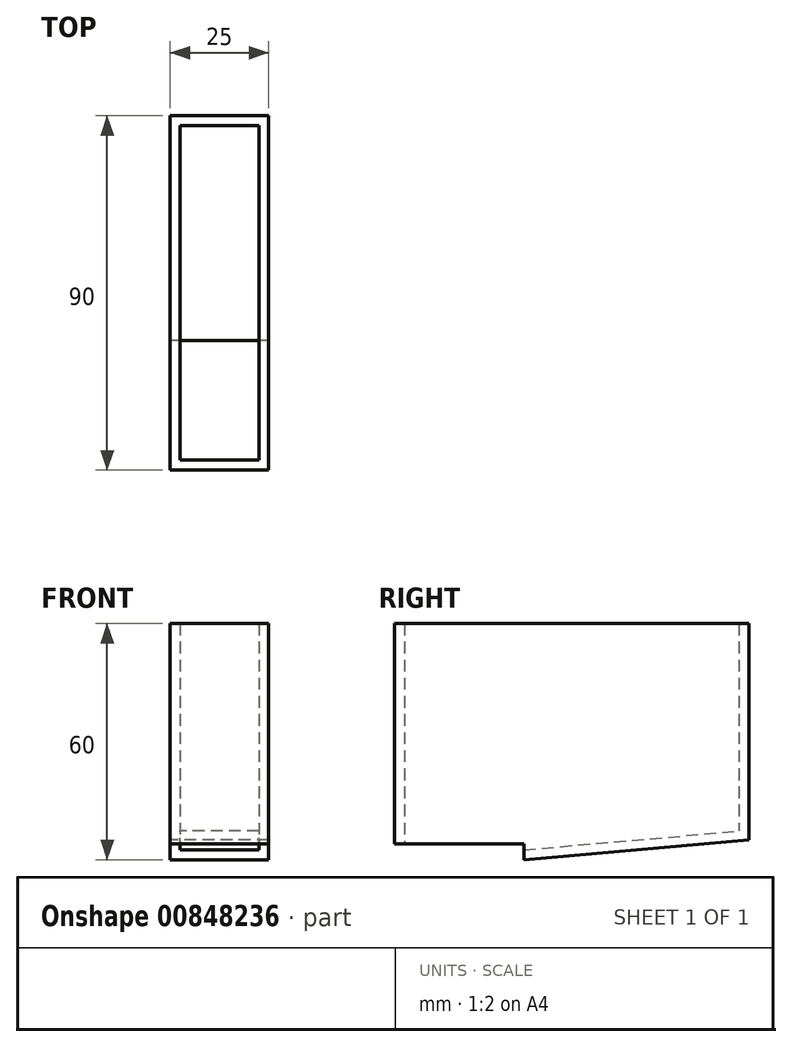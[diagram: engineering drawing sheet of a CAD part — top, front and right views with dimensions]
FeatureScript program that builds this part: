
annotation { "Feature Type Name" : "Feature", "Feature Type Description" : "" }
export const myFeature = defineFeature(function(context is Context, id is Id, definition is map)
    precondition{}
    {
        {
            var Q0;
            Q0=qCreatedBy(makeId("Front.planeOp"),FACE);
            var sketch = newSketch(context, id + "F0", { "sketchPlane" : qUnion([Q0])});
            skLineSegment(sketch, "E0.bottom", {"start": v(12.5, 30) * mm, "end": v(-12.5, 30) * mm});
            skLineSegment(sketch, "E0.top", {"start": v(12.5, -30) * mm, "end": v(-12.5, -30) * mm});
            skLineSegment(sketch, "E0.left", {"start": v(12.5, 30) * mm, "end": v(12.5, -30) * mm});
            skLineSegment(sketch, "E0.right", {"start": v(-12.5, 30) * mm, "end": v(-12.5, -30) * mm});
            skPoint(sketch, "E0.middle", {"position": v(0, 0) * mm});
            skSolve(sketch);
        }
        {
            var Q0;
            Q0=makeQuery(id+"F0.imprint","IMPRINT",FACE,{"disambiguationData":[TD([[makeQuery(id+"F0.imprint","IMPRINT",EDGE,{"derivedFrom":sQuery(id+"F0.wireOp",EDGE,"E0.bottom")}),1.0]])]});
            extrude(context, id + "F1", {"entities" : qUnion([Q0]), "depth" : 45 * mm, "offsetDistance" : 25 * mm, "hasSecondDirection" : true, "secondDirectionOppositeDirection" : true, "secondDirectionDepth" : 45 * mm});
        }
        {
            var Q0;
            Q0=makeQuery(id+"F1.opExtrude","SWEPT_FACE",FACE,{"disambiguationData":[OSD([sQuery(id+"F0.wireOp",EDGE,"E0.right")])]});
            var sketch = newSketch(context, id + "F2", { "sketchPlane" : qUnion([Q0])});
            skLineSegment(sketch, "E1", {"start": v(12.15, -30) * mm, "end": v(-45, -25) * mm});
            skLineSegment(sketch, "E2", {"start": v(-45, -25) * mm, "end": v(-45, -30) * mm});
            skLineSegment(sketch, "E3", {"start": v(-45, -30) * mm, "end": v(12.15, -30) * mm});
            skSolve(sketch);
        }
        {
            var Q0;
            Q0=makeQuery(id+"F2.imprint","IMPRINT",FACE,{"disambiguationData":[TD([[makeQuery(id+"F2.imprint","IMPRINT",EDGE,{"derivedFrom":sQuery(id+"F2.wireOp",EDGE,"E1")}),1.0]])]});
            extrude(context, id + "F3", {"entities" : qUnion([Q0]), "operationType" : NewBodyOperationType.REMOVE, "oppositeDirection" : true, "depth" : 25 * mm, "offsetDistance" : 25 * mm});
        }
        {
            var Q0;
            Q0=makeQuery(id+"F1.opExtrude","SWEPT_FACE",FACE,{"disambiguationData":[OSD([sQuery(id+"F0.wireOp",EDGE,"E0.right")])]});
            var sketch = newSketch(context, id + "F4", { "sketchPlane" : qUnion([Q0])});
            skLineSegment(sketch, "E4.bottom", {"start": v(45, -30) * mm, "end": v(12.15, -30) * mm});
            skLineSegment(sketch, "E4.top", {"start": v(45, -26) * mm, "end": v(12.15, -26) * mm});
            skLineSegment(sketch, "E4.left", {"start": v(45, -30) * mm, "end": v(45, -26) * mm});
            skLineSegment(sketch, "E4.right", {"start": v(12.15, -30) * mm, "end": v(12.15, -26) * mm});
            skSolve(sketch);
        }
        {
            var Q0;
            Q0=makeQuery(id+"F4.imprint","IMPRINT",FACE,{"disambiguationData":[TD([[makeQuery(id+"F4.imprint","IMPRINT",EDGE,{"derivedFrom":sQuery(id+"F4.wireOp",EDGE,"E4.bottom")}),-1.0]])]});
            extrude(context, id + "F5", {"entities" : qUnion([Q0]), "operationType" : NewBodyOperationType.REMOVE, "oppositeDirection" : true, "depth" : 25 * mm, "offsetDistance" : 25 * mm});
        }
        {
            var Q0;
            Q0=makeQuery(id+"F5.boolean.opBoolean","COPY",FACE,{"derivedFrom":makeQuery(id+"F5.opExtrude","SWEPT_FACE",FACE,{"disambiguationData":[OSD([sQuery(id+"F4.wireOp",EDGE,"E4.top")])]})});
            var Q1;
            Q1=makeQuery(id+"F5.boolean.opBoolean","COPY",FACE,{"derivedFrom":makeQuery(id+"F5.opExtrude","SWEPT_FACE",FACE,{"disambiguationData":[OSD([sQuery(id+"F4.wireOp",EDGE,"E4.right")])]})});
            var Q2;
            Q2=makeQuery(id+"F1.opExtrude","SWEPT_FACE",FACE,{"disambiguationData":[OSD([sQuery(id+"F0.wireOp",EDGE,"E0.bottom")])]});
            shell(context, id + "F6", {"entities" : qUnion([Q0, Q1, Q2]), "thickness" : 2.5 * mm});
        }
    });
